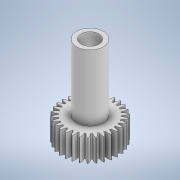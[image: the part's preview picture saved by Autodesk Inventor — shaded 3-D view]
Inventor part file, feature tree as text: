
AUTODESK INVENTOR PART (.ipt)
format: ipt  version: 2022 (Build 260153000, 153)  size: 289,792 bytes
history: native  units: mm
features: extrude x4, sketch x4, other x1, pattern_circular x1
ambient origin geometry x8: Origin, YZ Plane, XZ Plane, XY Plane, X Axis, Y Axis, Z Axis, Center Point
bodies: Body1 (feature_tree)
feature tree (10):
  other  "Bryła1"
  extrude  "Wyciągnięcie proste3"  Depth=20.0mm TaperAngle=0.0deg
  extrude  "Wyciągnięcie proste4"  Depth=24.0mm
  sketch  "Szkic3"
  sketch  "Szkic4"
  sketch  "Szkic1"
  sketch  "Szkic2"
  pattern_circular  "Szyk kołowy1"  [2 undecoded]
  extrude  "Wyciągnięcie proste1"  Depth=59.0mm TaperAngle=0.0deg
  extrude  "Wyciągnięcie proste2"  TaperAngle=0.0deg  [1 undecoded]
note: 3 required parameter values undecoded (feature->parameter linkage not recoverable at this tier; creation-order binding heuristic only, values carry confidence <= 0.55)
